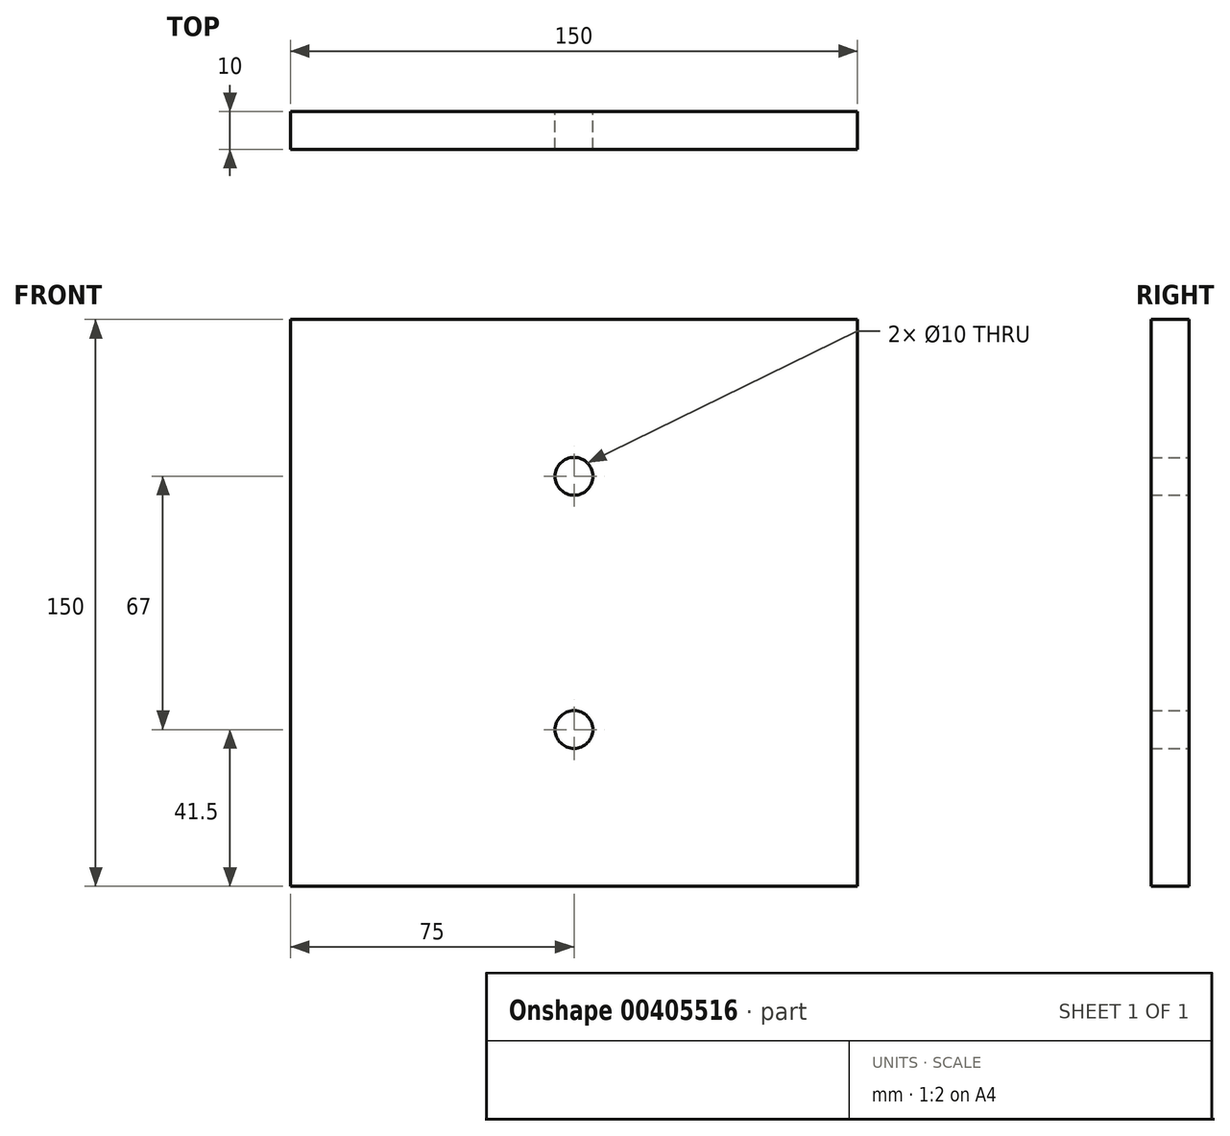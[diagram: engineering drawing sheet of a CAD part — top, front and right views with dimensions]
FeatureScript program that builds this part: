
annotation { "Feature Type Name" : "Feature", "Feature Type Description" : "" }
export const myFeature = defineFeature(function(context is Context, id is Id, definition is map)
    precondition{}
    {
        {
            var Q0;
            Q0=qCreatedBy(makeId("Front.planeOp"),FACE);
            var sketch = newSketch(context, id + "F0", { "sketchPlane" : qUnion([Q0])});
            skLineSegment(sketch, "E0.bottom", {"start": v(75, 75) * mm, "end": v(-75, 75) * mm});
            skLineSegment(sketch, "E0.top", {"start": v(75, -75) * mm, "end": v(-75, -75) * mm});
            skLineSegment(sketch, "E0.left", {"start": v(75, 75) * mm, "end": v(75, -75) * mm});
            skLineSegment(sketch, "E0.right", {"start": v(-75, 75) * mm, "end": v(-75, -75) * mm});
            skPoint(sketch, "E0.middle", {"position": v(0, 0) * mm});
            skCircle(sketch, "E1", {"center": v(0, 33.5) * mm, "radius": 5 * mm});
            skCircle(sketch, "E2.0.1.0", {"center": v(0, -33.5) * mm, "radius": 5 * mm});
            skLineSegment(sketch, "E2.direction1", {"start": v(0, 33.5) * mm, "end": v(70, 33.5) * mm, "construction": true});
            skLineSegment(sketch, "E2.direction2", {"start": v(0, 33.5) * mm, "end": v(0, -33.5) * mm, "construction": true});
            skLineSegment(sketch, "E3", {"start": v(0, 75) * mm, "end": v(0, -75) * mm, "construction": true});
            skSolve(sketch);
        }
        {
            var Q0;
            Q0=qSketchRegion(id+"F0",true);
            extrude(context, id + "F1", {"entities" : qUnion([Q0]), "depth" : 10 * mm});
        }
    });
